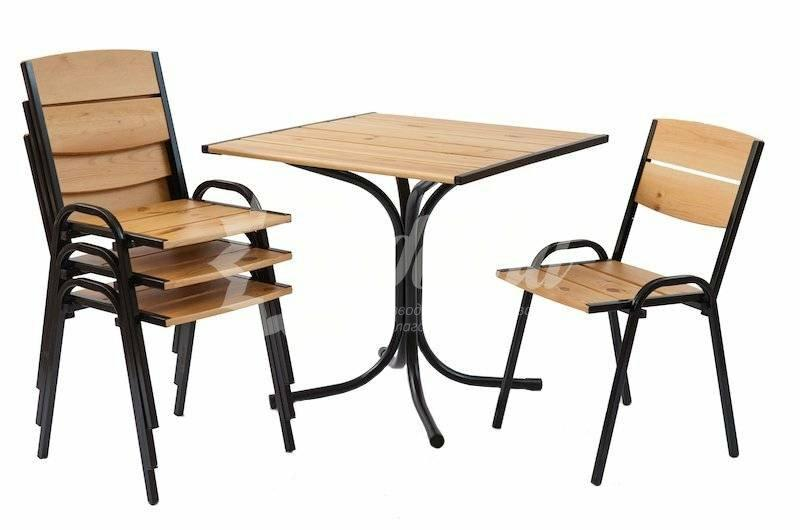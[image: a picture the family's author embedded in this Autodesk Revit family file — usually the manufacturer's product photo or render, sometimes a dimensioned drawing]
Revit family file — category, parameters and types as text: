
# Revit family: 10247 Комплект мебели «Петергоф» Хоббика
name_source: partatom
category: Антураж
revit_build: Autodesk Revit 2018 (Build: 20180423_1000(x64)
units: mm (PartAtom-declared; Revit-internal decimal feet)

## family parameters
Всегда вертикально = Да
Источник визуального образа = Геометрия семейства
На основе рабочей плоскости = Нет
Общий = Нет
При загрузке вырезать с полостями = Нет
Точка расчета площади = Нет

## types (2) — shared parameters
URL = https://hobbyka.ru
Артикул товара = Арт. 10247
Высота стола = 760 мм
Высота стула = 820 мм
Группа модели = Комплекты садовой мебели
Длина стола = 800 мм
Длина стула = 450 мм
Изготовитель = ООО «Хоббика»
Изображение типоразмера = Комплект мебели «Петергоф» Арт 10247.jpg
Материал изделия = Сталь, дерево
Цвет опор = Сталь
Цвет отделки = Дерево
Ширина стола = 800 мм
Ширина стула = 500 мм
zero-valued in all types: Высота

## per-type parameters (varying)
| type | На 2 стула | На 4 стула | Описание |
| Комплект мебели «Петергоф» на 4 стула | Нет | Да | Комплект мебели «Петергоф». Стол и 4 стула |
| Комплект мебели «Петергоф» на 2 стула | Да | Нет | Комплект мебели «Петергоф». Стол и 2 стула |
